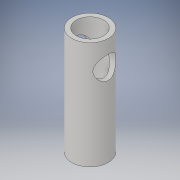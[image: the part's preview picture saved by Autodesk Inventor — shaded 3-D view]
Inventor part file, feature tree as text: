
AUTODESK INVENTOR PART (.ipt)
format: ipt  version: 2018 (Build 220112000, 112)  size: 124,928 bytes
history: native  units: in
note: dims shown in document units (in); Inventor stores cm internally (conversion verified against a paired STEP export)
features: extrude x3, sketch x3
ambient origin geometry x8: Origin, YZ Plane, XZ Plane, XY Plane, X Axis, Y Axis, Z Axis, Center Point
bodies: Solid1 (feature_tree)
feature tree (6):
  extrude  "Extrusion1"  Depth=1.476in TaperAngle=0.0deg
  extrude  "Extrusion3"  Depth=1.25in TaperAngle=0.0deg
  extrude  "Extrusion4"  Depth=1.133in
  sketch  "Sketch1"  dims[d0=0.5in d1=1.476in d2=0.5in d3=0.0in d4=0.0in]
  sketch  "Sketch3"  dims[d10=0.375in d11=1.25in d12=0.0in]
  sketch  "Sketch4"  dims[d13=0.312in d14=1.133in d15=0.25in d16=1.0in d17=0.0in]
